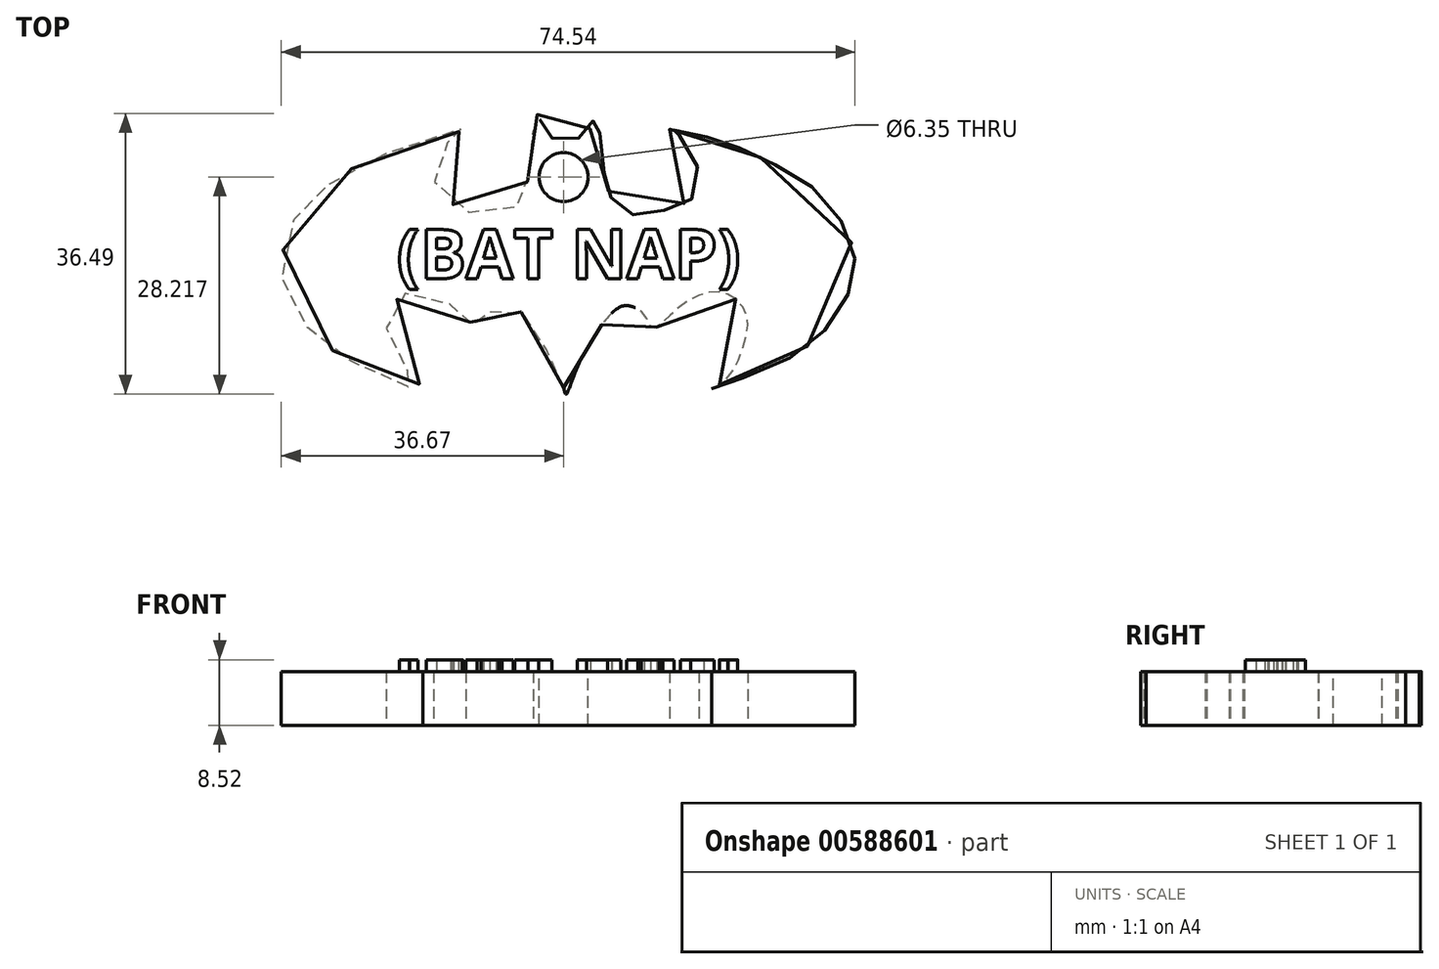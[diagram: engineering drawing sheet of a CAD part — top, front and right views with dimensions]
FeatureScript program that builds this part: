
annotation { "Feature Type Name" : "Feature", "Feature Type Description" : "" }
export const myFeature = defineFeature(function(context is Context, id is Id, definition is map)
    precondition{}
    {
        {
            var Q0;
            Q0=qCreatedBy(makeId("Top.planeOp"),FACE);
            var sketch = newSketch(context, id + "F0", { "sketchPlane" : qUnion([Q0])});
            skFitSpline(sketch, "E0", {"points": [v(0, -17.81) * mm, v(-1.16, -14.62) * mm, v(-3.42, -10.97) * mm, v(-5.35, -8.12) * mm, v(-7.91, -7) * mm, v(-10, -8.71) * mm, v(-10.85, -10.23) * mm, v(-11.88, -9.52) * mm, v(-12.63, -8.77) * mm, v(-14.71, -6.99) * mm, v(-19.23, -5.2) * mm, v(-22.35, -7.19) * mm, v(-23.01, -10.37) * mm, v(-21.55, -14.1) * mm, v(-18.3, -18.14) * mm, v(-23.1, -16.37) * mm, v(-29.48, -13.32) * mm, v(-34.04, -9.05) * mm, v(-36.63, -3.14) * mm, v(-34.9, 4.3) * mm, v(-31.38, 7.89) * mm, v(-26.6, 11.14) * mm, v(-13.52, 15.8) * mm, v(-12.72, 15.86) * mm, v(-13.72, 15.4) * mm, v(-16.24, 12.14) * mm, v(-16.8, 9.04) * mm, v(-14.71, 6.23) * mm, v(-8.45, 4.5) * mm, v(-5.48, 6.53) * mm, v(-4.73, 8.82) * mm, v(-4.1, 11.64) * mm, v(-3.94, 15.73) * mm, v(-3.9, 17) * mm, v(-3.57, 17.83) * mm, v(-2.04, 14.67) * mm, v(-1.37, 14.62) * mm, v(1.75, 14.68) * mm, v(2.9, 14.9) * mm, v(4.28, 17.58) * mm, v(4.88, 12.6) * mm, v(5.68, 8.49) * mm, v(6.6, 6.23) * mm, v(9.93, 4.5) * mm, v(14.1, 5.63) * mm, v(17.03, 7.16) * mm, v(16.9, 12.54) * mm, v(14.18, 15.6) * mm, v(13.78, 15.8) * mm, v(16.51, 15.25) * mm, v(21.08, 14.06) * mm, v(26.8, 11.54) * mm, v(33.3, 7.36) * mm, v(37.55, 0.58) * mm, v(37.29, -4.8) * mm, v(33.1, -11.24) * mm, v(25.13, -15.82) * mm, v(19.22, -17.94) * mm, v(20.88, -16.95) * mm, v(23.54, -11.84) * mm, v(23.74, -8.12) * mm, v(21.35, -5.66) * mm, v(18.1, -5.6) * mm, v(14.04, -8.18) * mm, v(11.62, -10.04) * mm, v(10.59, -8.45) * mm, v(8.93, -7.25) * mm, v(7.2, -7.39) * mm, v(2.69, -13.16) * mm, v(0.76, -17.81) * mm, v(0.58, -18.19) * mm, v(0.32, -18.65) * mm, v(0, -17.81) * mm]});
            skSolve(sketch);
        }
        {
            var Q0;
            Q0 = qSketchRegion(id + "F0", true);
            extrude(context, id + "F1", {"entities" : qUnion([Q0]), "depth" : 7 * mm, "offsetDistance" : 25.4 * mm});
        }
        {
            var Q0;
            Q0=makeQuery(id+"F1.opExtrude","CAP_FACE",FACE,{"disambiguationData":[OSD([sQuery(id+"F0.wireOp",EDGE,"E0")])],"isStart":false});
            var sketch = newSketch(context, id + "F2", { "sketchPlane" : qUnion([Q0])});
            skText(sketch, "E1", { "text": "(BAT NAP)", "fontName": "OpenSans-Bold.ttf"});
            const initialGuessF2  = {"E1": [-0.02168, -0.00361, 1, 0, 0.00642]};
            skSetInitialGuess(sketch, initialGuessF2);
            skSolve(sketch);
        }
        {
            var Q0;
            Q0 = qSketchRegion(id + "F2", true);
            extrude(context, id + "F3", {"entities" : qUnion([Q0]), "operationType" : NewBodyOperationType.ADD, "depth" : 1.52 * mm, "offsetDistance" : 25.4 * mm});
        }
        {
            var Q0;
            Q0=makeQuery(id+"F2.imprint","IMPRINT",FACE,{"disambiguationData":[TD([[makeQuery(id+"F2.imprint","IMPRINT",EDGE,{"derivedFrom":sQuery(id+"F2.wireOp",EDGE,"E1.sketch_text.stroke-0")}),1.0]])]});
            var sketch = newSketch(context, id + "F4", { "sketchPlane" : qUnion([Q0])});
            skCircle(sketch, "E2", {"center": v(0, 9.57) * mm, "radius": 3.26 * mm});
            skSolve(sketch);
        }
        {
            var Q0;
            Q0=sQuery(id+"F4.wireOp",VERTEX,"E2.center");
            var Q1;
            Q1=makeQuery(id+"F1.opExtrude","SWEPT_BODY",BODY,{"disambiguationData":[OSD([sQuery(id+"F0.wireOp",EDGE,"E0")])]});
            hole(context, id + "F5", {"style" : HoleStyle.SIMPLE, "endStyle" : HoleEndStyle.THROUGH, "holeDiameter" : 6.35 * mm, "majorDiameter" : 6.35 * mm, "isTappedThrough" : true, "tappedDepth" : 12.7 * mm, "tapClearance" : 3, "locations" : qUnion([Q0]), "scope" : qUnion([Q1])});
        }
    });
